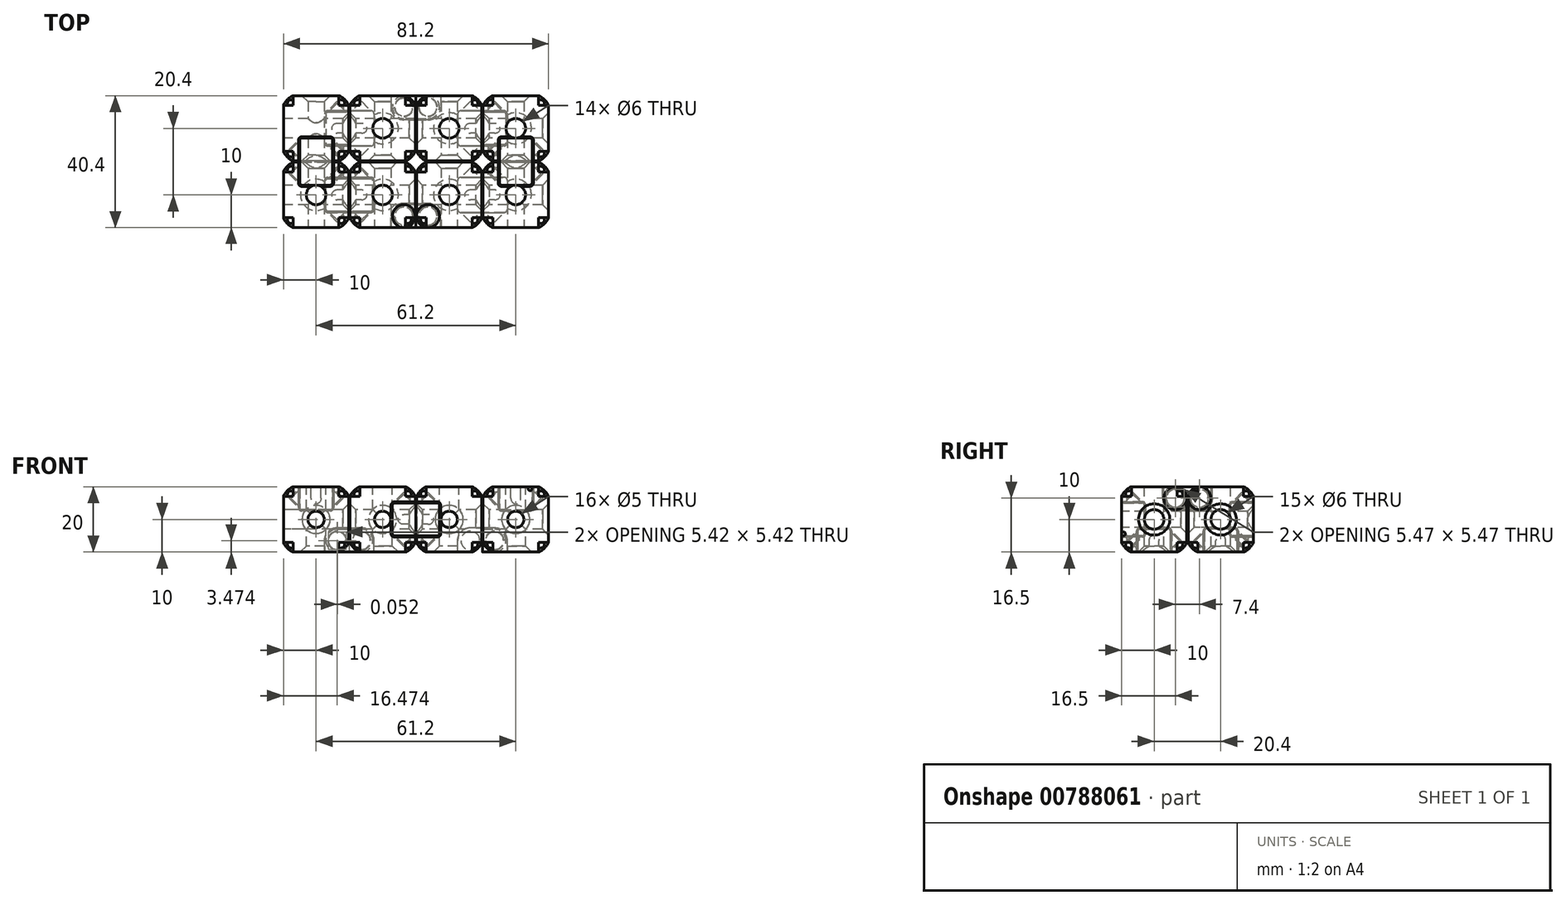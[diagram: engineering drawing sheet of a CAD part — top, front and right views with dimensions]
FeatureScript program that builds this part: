
annotation { "Feature Type Name" : "Feature", "Feature Type Description" : "" }
export const myFeature = defineFeature(function(context is Context, id is Id, definition is map)
    precondition{}
    {
        {
            assignVariable(context, id + "F0", {"name" : "cubeSize", "anyValue" : 20});
        }
        {
            assignVariable(context, id + "F1", {"name" : "hingeSize", "anyValue" : getVariable(context, 'cubeSize') / 2});
        }
        {
            assignVariable(context, id + "F2", {"name" : "hingeDiameter", "anyValue" : getVariable(context, 'hingeSize') / 2});
        }
        {
            assignVariable(context, id + "F3", {"name" : "minThickness", "anyValue" : 1});
        }
        {
            assignVariable(context, id + "F4", {"name" : "hingeGap", "anyValue" : .4});
        }
        {
            var Q0;
            Q0=qCreatedBy(makeId("Top.planeOp"),FACE);
            var sketch = newSketch(context, id + "F5", { "sketchPlane" : qUnion([Q0])});
            skLineSegment(sketch, "E0.bottom", {"start": v(10, -10) * mm, "end": v(-10, -10) * mm});
            skLineSegment(sketch, "E0.top", {"start": v(10, 10) * mm, "end": v(-10, 10) * mm});
            skLineSegment(sketch, "E0.left", {"start": v(10, -10) * mm, "end": v(10, 10) * mm});
            skLineSegment(sketch, "E0.right", {"start": v(-10, -10) * mm, "end": v(-10, 10) * mm});
            skPoint(sketch, "E0.middle", {"position": v(0, 0) * mm});
            skSolve(sketch);
        }
        {
            var Q0;
            Q0=qSketchRegion(id+"F5",true);
            extrude(context, id + "F6", {"entities" : qUnion([Q0]), "depth" : (getVariable(context, 'cubeSize')) * mm, "offsetDistance" : 25 * mm});
        }
        {
            var Q0;
            Q0=qCreatedBy(makeId("Front.planeOp"),FACE);
            var sketch = newSketch(context, id + "F7", { "sketchPlane" : qUnion([Q0])});
            skCircle(sketch, "E1", {"center": v(6.5, 3.5) * mm, "radius": 2.5 * mm});
            skLineSegment(sketch, "E2", {"start": v(6.5, 3.5) * mm, "end": v(9, 3.5) * mm, "construction": true});
            skLineSegment(sketch, "E3", {"start": v(9, 3.5) * mm, "end": v(10, 3.5) * mm, "construction": true});
            skLineSegment(sketch, "E4", {"start": v(6.5, 0) * mm, "end": v(6.5, 1) * mm, "construction": true});
            skLineSegment(sketch, "E5", {"start": v(6.5, 1) * mm, "end": v(6.5, 3.5) * mm, "construction": true});
            skLineSegment(sketch, "E6", {"start": v(10, 0) * mm, "end": v(2.6, 0) * mm});
            skLineSegment(sketch, "E7", {"start": v(2.6, 0) * mm, "end": v(2.6, 3.5) * mm});
            skLineSegment(sketch, "E8", {"start": v(10, 0) * mm, "end": v(10, 7.4) * mm});
            skLineSegment(sketch, "E9", {"start": v(10, 7.4) * mm, "end": v(6.5, 7.4) * mm});
            skArc(sketch, "E10", {"start": v(6.5, 7.4) * mm, "mid": v(3.74, 6.26) * mm, "end": v(2.6, 3.5) * mm});
            skSolve(sketch);
        }
        {
            var Q0;
            Q0=makeQuery(id+"F7.imprint","IMPRINT",FACE,{"disambiguationData":[TD([[makeQuery(id+"F7.imprint","IMPRINT",EDGE,{"derivedFrom":sQuery(id+"F7.wireOp",EDGE,"E1")}),-1.0]])]});
            var Q1;
            Q1=makeQuery(id+"F7.imprint","IMPRINT",FACE,{"disambiguationData":[TD([[makeQuery(id+"F7.imprint","IMPRINT",EDGE,{"derivedFrom":sQuery(id+"F7.wireOp",EDGE,"E1")}),1.0]])]});
            extrude(context, id + "F8", {"entities" : qUnion([Q0, Q1]), "operationType" : NewBodyOperationType.REMOVE, "oppositeDirection" : true, "depth" : (getVariable(context, 'hingeSize') + getVariable(context, 'hingeGap') * 2) * mm, "offsetDistance" : 25 * mm, "symmetric" : true});
        }
        {
            var Q0;
            Q0=makeQuery(id+"F6.opExtrude","CAP_VERTEX",VERTEX,{"disambiguationData":[OSD([sQuery(id+"F5.wireOp",EDGE,"E0.bottom"),sQuery(id+"F5.wireOp",EDGE,"E0.right")])],"isStart":false});
            var Q1;
            Q1=makeQuery(id+"F6.opExtrude","CAP_VERTEX",VERTEX,{"disambiguationData":[OSD([sQuery(id+"F5.wireOp",EDGE,"E0.bottom"),sQuery(id+"F5.wireOp",EDGE,"E0.left")])],"isStart":true});
            var Q2;
            Q2=makeQuery(id+"F6.opExtrude","CAP_VERTEX",VERTEX,{"disambiguationData":[OSD([sQuery(id+"F5.wireOp",EDGE,"E0.top"),sQuery(id+"F5.wireOp",EDGE,"E0.left")])],"isStart":true});
            cPlane(context, id + "F9", {"entities" : qUnion([Q0, Q1, Q2]), "cplaneType" : CPlaneType.THREE_POINT, "offset" : 25 * mm, "width" : 150 * mm, "height" : 150 * mm});
        }
        {
            var Q0;
            Q0=qCreatedBy(id+"F9.planeOp",FACE);
            var sketch = newSketch(context, id + "F10", { "sketchPlane" : qUnion([Q0])});
            skLineSegment(sketch, "E11", {"start": v(5.4, 0.78) * mm, "end": v(-5.4, 0.78) * mm});
            skLineSegment(sketch, "E12", {"start": v(-5.4, 0.78) * mm, "end": v(-8.3, -2.12) * mm});
            skLineSegment(sketch, "E13", {"start": v(-8.3, -2.12) * mm, "end": v(8.3, -2.12) * mm});
            skLineSegment(sketch, "E14", {"start": v(8.3, -2.12) * mm, "end": v(5.4, 0.78) * mm});
            skSolve(sketch);
        }
        {
            var Q0;
            Q0=makeQuery(id+"F10.imprint","IMPRINT",FACE,{"disambiguationData":[TD([[makeQuery(id+"F10.imprint","IMPRINT",EDGE,{"derivedFrom":sQuery(id+"F10.wireOp",EDGE,"E11")}),1.0]])]});
            var Q1;
            Q1=sQuery(id+"F10.wireOp",EDGE,"E13");
            revolve(context, id + "F11", {"operationType" : NewBodyOperationType.REMOVE, "entities" : qUnion([Q0]), "axis" : qUnion([Q1]), "revolveType" : RevolveType.FULL, "oppositeDirection" : true});
        }
        {
            var Q0;
            Q0=qCreatedBy(makeId("Right.planeOp"),FACE);
            var sketch = newSketch(context, id + "F12", { "sketchPlane" : qUnion([Q0])});
            skCircle(sketch, "E15", {"center": v(6.5, 16.5) * mm, "radius": 2.5 * mm});
            skLineSegment(sketch, "E16", {"start": v(2.6, 20) * mm, "end": v(10, 20) * mm});
            skLineSegment(sketch, "E17", {"start": v(10, 20) * mm, "end": v(10, 12.6) * mm});
            skLineSegment(sketch, "E18", {"start": v(10, 12.6) * mm, "end": v(6.5, 12.6) * mm});
            skLineSegment(sketch, "E19", {"start": v(2.6, 20) * mm, "end": v(2.6, 16.5) * mm});
            skLineSegment(sketch, "E20", {"start": v(6.5, 16.5) * mm, "end": v(9, 16.5) * mm, "construction": true});
            skLineSegment(sketch, "E21", {"start": v(9, 16.5) * mm, "end": v(10, 16.5) * mm, "construction": true});
            skLineSegment(sketch, "E22", {"start": v(6.5, 16.5) * mm, "end": v(6.5, 19) * mm, "construction": true});
            skLineSegment(sketch, "E23", {"start": v(6.5, 19) * mm, "end": v(6.5, 20) * mm, "construction": true});
            skArc(sketch, "E24", {"start": v(2.6, 16.5) * mm, "mid": v(3.74, 13.74) * mm, "end": v(6.5, 12.6) * mm});
            skSolve(sketch);
        }
        {
            var Q0;
            Q0=makeQuery(id+"F12.imprint","IMPRINT",FACE,{"disambiguationData":[TD([[makeQuery(id+"F12.imprint","IMPRINT",EDGE,{"derivedFrom":sQuery(id+"F12.wireOp",EDGE,"E15")}),1.0]])]});
            var Q1;
            Q1=makeQuery(id+"F12.imprint","IMPRINT",FACE,{"disambiguationData":[TD([[makeQuery(id+"F12.imprint","IMPRINT",EDGE,{"derivedFrom":sQuery(id+"F12.wireOp",EDGE,"E15")}),-1.0]])]});
            extrude(context, id + "F13", {"entities" : qUnion([Q0, Q1]), "operationType" : NewBodyOperationType.REMOVE, "depth" : (getVariable(context, 'hingeSize') + getVariable(context, 'hingeGap') * 2) * mm, "offsetDistance" : 25 * mm, "symmetric" : true});
        }
        {
            var Q0;
            Q0=makeQuery(id+"F6.opExtrude","CAP_VERTEX",VERTEX,{"disambiguationData":[OSD([sQuery(id+"F5.wireOp",EDGE,"E0.top"),sQuery(id+"F5.wireOp",EDGE,"E0.left")])],"isStart":false});
            var Q1;
            Q1=makeQuery(id+"F6.opExtrude","CAP_VERTEX",VERTEX,{"disambiguationData":[OSD([sQuery(id+"F5.wireOp",EDGE,"E0.top"),sQuery(id+"F5.wireOp",EDGE,"E0.right")])],"isStart":false});
            var Q2;
            Q2=makeQuery(id+"F6.opExtrude","CAP_VERTEX",VERTEX,{"disambiguationData":[OSD([sQuery(id+"F5.wireOp",EDGE,"E0.bottom"),sQuery(id+"F5.wireOp",EDGE,"E0.right")])],"isStart":true});
            cPlane(context, id + "F14", {"entities" : qUnion([Q0, Q1, Q2]), "cplaneType" : CPlaneType.THREE_POINT, "offset" : 25 * mm, "width" : 150 * mm, "height" : 150 * mm});
        }
        {
            var Q0;
            Q0=qCreatedBy(id+"F14.planeOp",FACE);
            var sketch = newSketch(context, id + "F15", { "sketchPlane" : qUnion([Q0])});
            skLineSegment(sketch, "E25", {"start": v(-8.3, 16.26) * mm, "end": v(8.3, 16.26) * mm});
            skLineSegment(sketch, "E26", {"start": v(8.3, 16.26) * mm, "end": v(5.4, 13.36) * mm});
            skLineSegment(sketch, "E27", {"start": v(5.4, 13.36) * mm, "end": v(-5.4, 13.36) * mm});
            skLineSegment(sketch, "E28", {"start": v(-5.4, 13.36) * mm, "end": v(-8.3, 16.26) * mm});
            skSolve(sketch);
        }
        {
            var Q0;
            Q0=qSketchRegion(id+"F15",true);
            var Q1;
            Q1=sQuery(id+"F15.wireOp",EDGE,"E25");
            revolve(context, id + "F16", {"operationType" : NewBodyOperationType.REMOVE, "entities" : qUnion([Q0]), "axis" : qUnion([Q1]), "revolveType" : RevolveType.FULL, "oppositeDirection" : true});
        }
        {
            var Q0;
            Q0=makeQuery(id+"F6.opExtrude","SWEPT_FACE",FACE,{"disambiguationData":[OSD([sQuery(id+"F5.wireOp",EDGE,"E0.right")])]});
            var Q1;
            Q1=makeQuery(id+"F6.opExtrude","SWEPT_FACE",FACE,{"disambiguationData":[OSD([sQuery(id+"F5.wireOp",EDGE,"E0.bottom")])]});
            var Q2;
            {var subQ0=sQuery(id+"F5.wireOp",EDGE,"E0.right");var subQ1=sQuery(id+"F5.wireOp",EDGE,"E0.top");Q2=makeQuery(id+"F13.boolean.opBoolean","SPLIT",EDGE,{"disambiguationData":[TD([makeQuery(id+"F6.opExtrude","SWEPT_FACE",FACE,{"disambiguationData":[OSD([subQ0])]})])],"derivedFrom":makeQuery(id+"F6.opExtrude","CAP_EDGE",EDGE,{"disambiguationData":[OSD([subQ1])],"isStart":false})});}
            var Q3;
            {var subQ0=sQuery(id+"F5.wireOp",EDGE,"E0.left");var subQ1=sQuery(id+"F5.wireOp",EDGE,"E0.top");Q3=makeQuery(id+"F13.boolean.opBoolean","SPLIT",EDGE,{"disambiguationData":[TD([makeQuery(id+"F6.opExtrude","SWEPT_FACE",FACE,{"disambiguationData":[OSD([subQ0])]})])],"derivedFrom":makeQuery(id+"F6.opExtrude","CAP_EDGE",EDGE,{"disambiguationData":[OSD([subQ1])],"isStart":false})});}
            var Q4;
            Q4=makeQuery(id+"F6.opExtrude","CAP_EDGE",EDGE,{"disambiguationData":[OSD([sQuery(id+"F5.wireOp",EDGE,"E0.left")])],"isStart":false});
            var Q5;
            Q5=makeQuery(id+"F6.opExtrude","SWEPT_EDGE",EDGE,{"disambiguationData":[OSD([sQuery(id+"F5.wireOp",EDGE,"E0.top"),sQuery(id+"F5.wireOp",EDGE,"E0.left")])]});
            var Q6;
            {var subQ0=sQuery(id+"F5.wireOp",EDGE,"E0.left");var subQ1=sQuery(id+"F5.wireOp",EDGE,"E0.top");Q6=makeQuery(id+"F8.boolean.opBoolean","SPLIT",EDGE,{"disambiguationData":[TD([makeQuery(id+"F6.opExtrude","SWEPT_FACE",FACE,{"disambiguationData":[OSD([subQ1])]})])],"derivedFrom":makeQuery(id+"F6.opExtrude","CAP_EDGE",EDGE,{"disambiguationData":[OSD([subQ0])],"isStart":true})});}
            var Q7;
            Q7=makeQuery(id+"F6.opExtrude","CAP_EDGE",EDGE,{"disambiguationData":[OSD([sQuery(id+"F5.wireOp",EDGE,"E0.top")])],"isStart":true});
            var Q8;
            {var subQ0=sQuery(id+"F5.wireOp",EDGE,"E0.bottom");var subQ1=sQuery(id+"F5.wireOp",EDGE,"E0.left");Q8=makeQuery(id+"F8.boolean.opBoolean","SPLIT",EDGE,{"disambiguationData":[TD([makeQuery(id+"F6.opExtrude","SWEPT_FACE",FACE,{"disambiguationData":[OSD([subQ0])]})])],"derivedFrom":makeQuery(id+"F6.opExtrude","CAP_EDGE",EDGE,{"disambiguationData":[OSD([subQ1])],"isStart":true})});}
            fillet(context, id + "F17", {"entities" : qUnion([Q0, Q1, Q2, Q3, Q4, Q5, Q6, Q7, Q8]), "radius" : (getVariable(context, 'hingeDiameter') / 2 + getVariable(context, 'minThickness') - .5) * mm, "tangentPropagation" : true, "rho" : .2, "crossSection" : FilletCrossSection.CONIC, "allowEdgeOverflow" : false});
        }
        {
            var Q0;
            Q0=makeQuery(id+"F8.boolean.opBoolean","COPY",EDGE,{"derivedFrom":makeQuery(id+"F8.opExtrude","CAP_EDGE",EDGE,{"disambiguationData":[OSD([sQuery(id+"F7.wireOp",EDGE,"E7")])],"isStart":true})});
            var Q1;
            Q1=makeQuery(id+"F8.boolean.opBoolean","COPY",EDGE,{"derivedFrom":makeQuery(id+"F8.opExtrude","CAP_EDGE",EDGE,{"disambiguationData":[OSD([sQuery(id+"F7.wireOp",EDGE,"E7")])],"isStart":false})});
            var Q2;
            Q2=makeQuery(id+"F13.boolean.opBoolean","COPY",EDGE,{"derivedFrom":makeQuery(id+"F13.opExtrude","CAP_EDGE",EDGE,{"disambiguationData":[OSD([sQuery(id+"F12.wireOp",EDGE,"E18")])],"isStart":false})});
            var Q3;
            Q3=makeQuery(id+"F13.boolean.opBoolean","COPY",EDGE,{"derivedFrom":makeQuery(id+"F13.opExtrude","CAP_EDGE",EDGE,{"disambiguationData":[OSD([sQuery(id+"F12.wireOp",EDGE,"E18")])],"isStart":true})});
            fillet(context, id + "F18", {"entities" : qUnion([Q0, Q1, Q2, Q3]), "radius" : (getVariable(context, 'minThickness')) * mm, "tangentPropagation" : true, "allowEdgeOverflow" : false});
        }
        {
            var Q0;
            Q0=qCreatedBy(makeId("Front.planeOp"),FACE);
            var sketch = newSketch(context, id + "F19", { "sketchPlane" : qUnion([Q0])});
            skCircle(sketch, "E29", {"center": v(6.5, 3.5) * mm, "radius": 2.5 * mm, "construction": true});
            skArc(sketch, "E30", {"start": v(6.5, 7) * mm, "mid": v(3, 3.5) * mm, "end": v(6.5, 0) * mm});
            skArc(sketch, "E31", {"start": v(13.9, 0) * mm, "mid": v(17.4, 3.5) * mm, "end": v(13.9, 7) * mm});
            skLineSegment(sketch, "E32", {"start": v(6.5, 3.5) * mm, "end": v(10, 3.5) * mm, "construction": true});
            skCircle(sketch, "E33", {"center": v(13.9, 3.5) * mm, "radius": 2.5 * mm, "construction": true});
            skLineSegment(sketch, "E34", {"start": v(10, 3.5) * mm, "end": v(10.4, 3.5) * mm, "construction": true});
            skLineSegment(sketch, "E35", {"start": v(10.4, 3.5) * mm, "end": v(13.9, 3.5) * mm, "construction": true});
            skLineSegment(sketch, "E36", {"start": v(10.2, 0) * mm, "end": v(10.2, 3.5) * mm});
            skLineSegment(sketch, "E37", {"start": v(10.2, 3.5) * mm, "end": v(10.2, 7) * mm});
            skLineSegment(sketch, "E38", {"start": v(13.9, 0) * mm, "end": v(6.5, 0) * mm});
            skLineSegment(sketch, "E39", {"start": v(13.9, 7) * mm, "end": v(6.5, 7) * mm});
            skSolve(sketch);
        }
        {
            var Q0;
            Q0=makeQuery(id+"F19.imprint","IMPRINT",FACE,{"disambiguationData":[TD([[makeQuery(id+"F19.imprint","IMPRINT",EDGE,{"derivedFrom":sQuery(id+"F19.wireOp",EDGE,"E30")}),1.0]])]});
            extrude(context, id + "F20", {"entities" : qUnion([Q0]), "depth" : (getVariable(context, 'hingeSize')) * mm, "offsetDistance" : 25 * mm, "symmetric" : true});
        }
        {
            var Q0;
            Q0=qCreatedBy(id+"F9.planeOp",FACE);
            var sketch = newSketch(context, id + "F21", { "sketchPlane" : qUnion([Q0])});
            skLineSegment(sketch, "E40", {"start": v(7.73, -2.12) * mm, "end": v(4.83, 0.78) * mm});
            skLineSegment(sketch, "E41", {"start": v(4.83, 0.78) * mm, "end": v(-4.83, 0.78) * mm});
            skLineSegment(sketch, "E42", {"start": v(-4.83, 0.78) * mm, "end": v(-7.73, -2.12) * mm});
            skLineSegment(sketch, "E43", {"start": v(-7.73, -2.12) * mm, "end": v(7.73, -2.12) * mm});
            skSolve(sketch);
        }
        {
            var Q0;
            Q0=qSketchRegion(id+"F21",true);
            var Q1;
            Q1=sQuery(id+"F21.wireOp",EDGE,"E43");
            revolve(context, id + "F22", {"operationType" : NewBodyOperationType.ADD, "entities" : qUnion([Q0]), "axis" : qUnion([Q1]), "revolveType" : RevolveType.FULL});
        }
        {
            var Q0;
            Q0=qCreatedBy(makeId("Right.planeOp"),FACE);
            var sketch = newSketch(context, id + "F23", { "sketchPlane" : qUnion([Q0])});
            skCircle(sketch, "E44", {"center": v(6.5, 16.5) * mm, "radius": 2.9 * mm, "construction": true});
            skArc(sketch, "E45", {"start": v(6.5, 20) * mm, "mid": v(3, 16.5) * mm, "end": v(6.5, 13) * mm});
            skArc(sketch, "E46", {"start": v(13.9, 13) * mm, "mid": v(17.4, 16.5) * mm, "end": v(13.9, 20) * mm});
            skLineSegment(sketch, "E47", {"start": v(6.5, 16.5) * mm, "end": v(10, 16.5) * mm, "construction": true});
            skCircle(sketch, "E48", {"center": v(13.9, 16.5) * mm, "radius": 2.5 * mm, "construction": true});
            skLineSegment(sketch, "E49", {"start": v(10, 16.5) * mm, "end": v(10.4, 16.5) * mm, "construction": true});
            skLineSegment(sketch, "E50", {"start": v(10.4, 16.5) * mm, "end": v(13.9, 16.5) * mm, "construction": true});
            skLineSegment(sketch, "E51", {"start": v(10.2, 13) * mm, "end": v(10.2, 16.5) * mm});
            skLineSegment(sketch, "E52", {"start": v(10.2, 16.5) * mm, "end": v(10.2, 20) * mm});
            skLineSegment(sketch, "E53", {"start": v(13.9, 13) * mm, "end": v(6.5, 13) * mm});
            skLineSegment(sketch, "E54", {"start": v(13.9, 20) * mm, "end": v(6.5, 20) * mm});
            skSolve(sketch);
        }
        {
            var Q0;
            {var subQ3=sQuery(id+"F23.wireOp",EDGE,"E45");Q0=makeQuery(id+"F23.imprint","IMPRINT",FACE,{"disambiguationData":[TD([[makeQuery(id+"F23.imprint","IMPRINT",EDGE,{"derivedFrom":subQ3}),1.0]])]});}
            extrude(context, id + "F24", {"entities" : qUnion([Q0]), "depth" : (getVariable(context, 'hingeSize')) * mm, "offsetDistance" : 25 * mm, "symmetric" : true});
        }
        {
            var Q0;
            Q0=makeQuery(id+"F20.opExtrude","CAP_EDGE",EDGE,{"disambiguationData":[OSD([sQuery(id+"F19.wireOp",EDGE,"E38")])],"isStart":false});
            var Q1;
            Q1=makeQuery(id+"F20.opExtrude","CAP_EDGE",EDGE,{"disambiguationData":[OSD([sQuery(id+"F19.wireOp",EDGE,"E38")])],"isStart":true});
            var Q2;
            Q2=makeQuery(id+"F24.opExtrude","CAP_EDGE",EDGE,{"disambiguationData":[OSD([sQuery(id+"F23.wireOp",EDGE,"E54")])],"isStart":false});
            var Q3;
            Q3=makeQuery(id+"F24.opExtrude","CAP_EDGE",EDGE,{"disambiguationData":[OSD([sQuery(id+"F23.wireOp",EDGE,"E54")])],"isStart":true});
            fillet(context, id + "F25", {"entities" : qUnion([Q0, Q1, Q2, Q3]), "radius" : (getVariable(context, 'minThickness') - getVariable(context, 'hingeGap')) * mm, "tangentPropagation" : true, "allowEdgeOverflow" : false});
        }
        {
            var Q0;
            Q0=qCreatedBy(id+"F14.planeOp",FACE);
            var sketch = newSketch(context, id + "F26", { "sketchPlane" : qUnion([Q0])});
            skLineSegment(sketch, "E55", {"start": v(-7.73, 16.26) * mm, "end": v(7.73, 16.26) * mm});
            skLineSegment(sketch, "E56", {"start": v(7.73, 16.26) * mm, "end": v(4.83, 13.36) * mm});
            skLineSegment(sketch, "E57", {"start": v(4.83, 13.36) * mm, "end": v(-4.83, 13.36) * mm});
            skLineSegment(sketch, "E58", {"start": v(-4.83, 13.36) * mm, "end": v(-7.73, 16.26) * mm});
            skSolve(sketch);
        }
        {
            var Q0;
            Q0=makeQuery(id+"F26.imprint","IMPRINT",FACE,{"disambiguationData":[TD([[makeQuery(id+"F26.imprint","IMPRINT",EDGE,{"derivedFrom":sQuery(id+"F26.wireOp",EDGE,"E55")}),-1.0]])]});
            var Q1;
            Q1=sQuery(id+"F26.wireOp",EDGE,"E55");
            revolve(context, id + "F27", {"operationType" : NewBodyOperationType.ADD, "entities" : qUnion([Q0]), "axis" : qUnion([Q1]), "revolveType" : RevolveType.FULL});
        }
        {
            var Q0;
            Q0=makeQuery(id+"F20.opExtrude","SWEPT_FACE",FACE,{"disambiguationData":[OSD([sQuery(id+"F19.wireOp",EDGE,"E36"),sQuery(id+"F19.wireOp",EDGE,"E37")])]});
            var sketch = newSketch(context, id + "F28", { "sketchPlane" : qUnion([Q0])});
            skLineSegment(sketch, "E59", {"start": v(-7.63, -0.2) * mm, "end": v(6.67, -0.2) * mm, "construction": true});
            skSolve(sketch);
        }
        {
            var Q0;
            Q0=makeQuery(id+"F6.opExtrude","SWEPT_BODY",BODY,{"disambiguationData":[OSD([sQuery(id+"F5.wireOp",EDGE,"E0.bottom"),sQuery(id+"F5.wireOp",EDGE,"E0.top"),sQuery(id+"F5.wireOp",EDGE,"E0.left"),sQuery(id+"F5.wireOp",EDGE,"E0.right")])]});
            var Q1;
            Q1=makeQuery(id+"F24.opExtrude","SWEPT_BODY",BODY,{"disambiguationData":[OSD([sQuery(id+"F23.wireOp",EDGE,"E45"),sQuery(id+"F23.wireOp",EDGE,"E51"),sQuery(id+"F23.wireOp",EDGE,"E52"),sQuery(id+"F23.wireOp",EDGE,"E53"),sQuery(id+"F23.wireOp",EDGE,"E54")])]});
            var Q2;
            Q2=sQuery(id+"F28.wireOp",EDGE,"E59");
            circularPattern(context, id + "F29", {"entities" : qUnion([Q0, Q1]), "axis" : qUnion([Q2]), "angle" : 90 * degree, "instanceCount" : 2});
        }
        {
            var Q0;
            Q0=makeQuery(id+"F29.opPattern","COPY",BODY,{"derivedFrom":makeQuery(id+"F6.opExtrude","SWEPT_BODY",BODY,{"disambiguationData":[OSD([sQuery(id+"F5.wireOp",EDGE,"E0.bottom"),sQuery(id+"F5.wireOp",EDGE,"E0.top"),sQuery(id+"F5.wireOp",EDGE,"E0.left"),sQuery(id+"F5.wireOp",EDGE,"E0.right")])]}),"instanceName":"1"});
            var Q1;
            Q1=makeQuery(id+"F29.opPattern","COPY",BODY,{"derivedFrom":makeQuery(id+"F24.opExtrude","SWEPT_BODY",BODY,{"disambiguationData":[OSD([sQuery(id+"F23.wireOp",EDGE,"E45"),sQuery(id+"F23.wireOp",EDGE,"E51"),sQuery(id+"F23.wireOp",EDGE,"E52"),sQuery(id+"F23.wireOp",EDGE,"E53"),sQuery(id+"F23.wireOp",EDGE,"E54")])]}),"instanceName":"1"});
            var Q2;
            Q2=qCreatedBy(makeId("Front.planeOp"),FACE);
            mirror(context, id + "F30", {"entities" : qUnion([Q0, Q1]), "mirrorPlane" : qUnion([Q2])});
        }
        {
            var Q0;
            Q0=makeQuery(id+"F29.opPattern","COPY",BODY,{"derivedFrom":makeQuery(id+"F24.opExtrude","SWEPT_BODY",BODY,{"disambiguationData":[OSD([sQuery(id+"F23.wireOp",EDGE,"E45"),sQuery(id+"F23.wireOp",EDGE,"E51"),sQuery(id+"F23.wireOp",EDGE,"E52"),sQuery(id+"F23.wireOp",EDGE,"E53"),sQuery(id+"F23.wireOp",EDGE,"E54")])]}),"instanceName":"1"});
            var Q1;
            Q1=makeQuery(id+"F29.opPattern","COPY",BODY,{"derivedFrom":makeQuery(id+"F6.opExtrude","SWEPT_BODY",BODY,{"disambiguationData":[OSD([sQuery(id+"F5.wireOp",EDGE,"E0.bottom"),sQuery(id+"F5.wireOp",EDGE,"E0.top"),sQuery(id+"F5.wireOp",EDGE,"E0.left"),sQuery(id+"F5.wireOp",EDGE,"E0.right")])]}),"instanceName":"1"});
            deleteBodies(context, id + "F31", {"entities" : qUnion([Q0, Q1])});
        }
        {
            var Q0;
            Q0=makeQuery(id+"F20.opExtrude","SWEPT_BODY",BODY,{"disambiguationData":[OSD([sQuery(id+"F19.wireOp",EDGE,"E30"),sQuery(id+"F19.wireOp",EDGE,"E36"),sQuery(id+"F19.wireOp",EDGE,"E37"),sQuery(id+"F19.wireOp",EDGE,"E38"),sQuery(id+"F19.wireOp",EDGE,"E39")])]});
            var Q1;
            Q1=makeQuery(id+"F20.opExtrude","SWEPT_FACE",FACE,{"disambiguationData":[OSD([sQuery(id+"F19.wireOp",EDGE,"E36"),sQuery(id+"F19.wireOp",EDGE,"E37")])]});
            mirror(context, id + "F32", {"operationType" : NewBodyOperationType.ADD, "entities" : qUnion([Q0]), "mirrorPlane" : qUnion([Q1])});
        }
        {
            var Q0;
            {var subQ0=sQuery(id+"F5.wireOp",EDGE,"E0.left");var subQ1=makeQuery(id+"F6.opExtrude","SWEPT_FACE",FACE,{"disambiguationData":[OSD([subQ0])]});var subQ2=sQuery(id+"F5.wireOp",EDGE,"E0.bottom");Q0=makeQuery(id+"F30.opPattern","COPY",VERTEX,{"derivedFrom":makeQuery(id+"F29.opPattern","COPY",VERTEX,{"derivedFrom":makeQuery(id+"F17.opFillet","BLEND_VERTEX",VERTEX,{"blendedFrom":[makeQuery(id+"F6.opExtrude","CAP_VERTEX",VERTEX,{"disambiguationData":[OSD([subQ2,subQ0])],"isStart":true}),makeQuery(id+"F6.opExtrude","SWEPT_EDGE",EDGE,{"disambiguationData":[OSD([subQ2,subQ0])]}),makeQuery(id+"F8.boolean.opBoolean","SPLIT",EDGE,{"disambiguationData":[TD([makeQuery(id+"F6.opExtrude","SWEPT_FACE",FACE,{"disambiguationData":[OSD([subQ2])]})])],"derivedFrom":makeQuery(id+"F6.opExtrude","CAP_EDGE",EDGE,{"disambiguationData":[OSD([subQ0])],"isStart":true})}),subQ1],"blendedInto":[subQ1]}),"instanceName":"1"}),"instanceName":"1"});}
            var Q1;
            {var subQ0=sQuery(id+"F5.wireOp",EDGE,"E0.left");var subQ1=sQuery(id+"F5.wireOp",EDGE,"E0.top");Q1=makeQuery(id+"F30.opPattern","COPY",VERTEX,{"derivedFrom":makeQuery(id+"F29.opPattern","COPY",VERTEX,{"derivedFrom":makeQuery(id+"F17.opFillet","BLEND_VERTEX",VERTEX,{"blendedFrom":[makeQuery(id+"F6.opExtrude","CAP_VERTEX",VERTEX,{"disambiguationData":[OSD([subQ1,subQ0])],"isStart":false}),makeQuery(id+"F6.opExtrude","SWEPT_EDGE",EDGE,{"disambiguationData":[OSD([subQ1,subQ0])]}),makeQuery(id+"F6.opExtrude","CAP_EDGE",EDGE,{"disambiguationData":[OSD([subQ0])],"isStart":false}),makeQuery(id+"F6.opExtrude","SWEPT_FACE",FACE,{"disambiguationData":[OSD([subQ0])]})],"blendedInto":[makeQuery(id+"F6.opExtrude","SWEPT_FACE",FACE,{"disambiguationData":[OSD([subQ0])]})]}),"instanceName":"1"}),"instanceName":"1"});}
            var Q2;
            {var subQ0=sQuery(id+"F5.wireOp",EDGE,"E0.right");var subQ1=sQuery(id+"F5.wireOp",EDGE,"E0.top");Q2=makeQuery(id+"F30.opPattern","COPY",VERTEX,{"derivedFrom":makeQuery(id+"F29.opPattern","COPY",VERTEX,{"derivedFrom":makeQuery(id+"F17.opFillet","BLEND_VERTEX",VERTEX,{"blendedFrom":[makeQuery(id+"F6.opExtrude","CAP_VERTEX",VERTEX,{"disambiguationData":[OSD([subQ1,subQ0])],"isStart":false}),makeQuery(id+"F6.opExtrude","SWEPT_EDGE",EDGE,{"disambiguationData":[OSD([subQ1,subQ0])]}),makeQuery(id+"F6.opExtrude","CAP_EDGE",EDGE,{"disambiguationData":[OSD([subQ0])],"isStart":false}),makeQuery(id+"F6.opExtrude","SWEPT_FACE",FACE,{"disambiguationData":[OSD([subQ0])]})],"blendedInto":[makeQuery(id+"F6.opExtrude","SWEPT_FACE",FACE,{"disambiguationData":[OSD([subQ0])]})]}),"instanceName":"1"}),"instanceName":"1"});}
            cPlane(context, id + "F33", {"entities" : qUnion([Q0, Q1, Q2]), "cplaneType" : CPlaneType.THREE_POINT, "offset" : 25 * mm, "width" : 150 * mm, "height" : 150 * mm});
        }
        {
            var Q0;
            Q0=qCreatedBy(id+"F33.planeOp",FACE);
            var sketch = newSketch(context, id + "F34", { "sketchPlane" : qUnion([Q0])});
            skLineSegment(sketch, "E60", {"start": v(-23.62, 17.73) * mm, "end": v(-23.62, 2.27) * mm, "construction": true});
            skSolve(sketch);
        }
        {
            var Q0;
            Q0=makeQuery(id+"F30.opPattern","COPY",BODY,{"derivedFrom":makeQuery(id+"F29.opPattern","COPY",BODY,{"derivedFrom":makeQuery(id+"F24.opExtrude","SWEPT_BODY",BODY,{"disambiguationData":[OSD([sQuery(id+"F23.wireOp",EDGE,"E45"),sQuery(id+"F23.wireOp",EDGE,"E51"),sQuery(id+"F23.wireOp",EDGE,"E52"),sQuery(id+"F23.wireOp",EDGE,"E53"),sQuery(id+"F23.wireOp",EDGE,"E54")])]}),"instanceName":"1"}),"instanceName":"1"});
            var Q1;
            Q1=sQuery(id+"F34.wireOp",EDGE,"E60");
            circularPattern(context, id + "F35", {"entities" : qUnion([Q0]), "axis" : qUnion([Q1]), "angle" : 90 * degree, "instanceCount" : 2, "oppositeDirection" : true});
        }
        {
            var Q0;
            Q0=makeQuery(id+"F30.opPattern","COPY",BODY,{"derivedFrom":makeQuery(id+"F29.opPattern","COPY",BODY,{"derivedFrom":makeQuery(id+"F24.opExtrude","SWEPT_BODY",BODY,{"disambiguationData":[OSD([sQuery(id+"F23.wireOp",EDGE,"E45"),sQuery(id+"F23.wireOp",EDGE,"E51"),sQuery(id+"F23.wireOp",EDGE,"E52"),sQuery(id+"F23.wireOp",EDGE,"E53"),sQuery(id+"F23.wireOp",EDGE,"E54")])]}),"instanceName":"1"}),"instanceName":"1"});
            deleteBodies(context, id + "F36", {"entities" : qUnion([Q0])});
        }
        {
            var Q0;
            Q0=makeQuery(id+"F24.opExtrude","SWEPT_BODY",BODY,{"disambiguationData":[OSD([sQuery(id+"F23.wireOp",EDGE,"E45"),sQuery(id+"F23.wireOp",EDGE,"E51"),sQuery(id+"F23.wireOp",EDGE,"E52"),sQuery(id+"F23.wireOp",EDGE,"E53"),sQuery(id+"F23.wireOp",EDGE,"E54")])]});
            var Q1;
            Q1=makeQuery(id+"F6.opExtrude","SWEPT_BODY",BODY,{"disambiguationData":[OSD([sQuery(id+"F5.wireOp",EDGE,"E0.bottom"),sQuery(id+"F5.wireOp",EDGE,"E0.top"),sQuery(id+"F5.wireOp",EDGE,"E0.left"),sQuery(id+"F5.wireOp",EDGE,"E0.right")])]});
            var Q2;
            Q2=makeQuery(id+"F20.opExtrude","SWEPT_BODY",BODY,{"disambiguationData":[OSD([sQuery(id+"F19.wireOp",EDGE,"E30"),sQuery(id+"F19.wireOp",EDGE,"E36"),sQuery(id+"F19.wireOp",EDGE,"E37"),sQuery(id+"F19.wireOp",EDGE,"E38"),sQuery(id+"F19.wireOp",EDGE,"E39")])]});
            var Q3;
            Q3=makeQuery(id+"F30.opPattern","COPY",BODY,{"derivedFrom":makeQuery(id+"F29.opPattern","COPY",BODY,{"derivedFrom":makeQuery(id+"F6.opExtrude","SWEPT_BODY",BODY,{"disambiguationData":[OSD([sQuery(id+"F5.wireOp",EDGE,"E0.bottom"),sQuery(id+"F5.wireOp",EDGE,"E0.top"),sQuery(id+"F5.wireOp",EDGE,"E0.left"),sQuery(id+"F5.wireOp",EDGE,"E0.right")])]}),"instanceName":"1"}),"instanceName":"1"});
            var Q4;
            Q4=makeQuery(id+"F35.opPattern","COPY",BODY,{"derivedFrom":makeQuery(id+"F30.opPattern","COPY",BODY,{"derivedFrom":makeQuery(id+"F29.opPattern","COPY",BODY,{"derivedFrom":makeQuery(id+"F24.opExtrude","SWEPT_BODY",BODY,{"disambiguationData":[OSD([sQuery(id+"F23.wireOp",EDGE,"E45"),sQuery(id+"F23.wireOp",EDGE,"E51"),sQuery(id+"F23.wireOp",EDGE,"E52"),sQuery(id+"F23.wireOp",EDGE,"E53"),sQuery(id+"F23.wireOp",EDGE,"E54")])]}),"instanceName":"1"}),"instanceName":"1"}),"instanceName":"1"});
            var Q5;
            Q5=makeQuery(id+"F24.opExtrude","SWEPT_FACE",FACE,{"disambiguationData":[OSD([sQuery(id+"F23.wireOp",EDGE,"E51"),sQuery(id+"F23.wireOp",EDGE,"E52")])]});
            mirror(context, id + "F37", {"operationType" : NewBodyOperationType.ADD, "entities" : qUnion([Q0, Q1, Q2, Q3, Q4]), "mirrorPlane" : qUnion([Q5])});
        }
        {
            var Q0;
            Q0=makeQuery(id+"F35.opPattern","COPY",BODY,{"derivedFrom":makeQuery(id+"F30.opPattern","COPY",BODY,{"derivedFrom":makeQuery(id+"F29.opPattern","COPY",BODY,{"derivedFrom":makeQuery(id+"F24.opExtrude","SWEPT_BODY",BODY,{"disambiguationData":[OSD([sQuery(id+"F23.wireOp",EDGE,"E45"),sQuery(id+"F23.wireOp",EDGE,"E51"),sQuery(id+"F23.wireOp",EDGE,"E52"),sQuery(id+"F23.wireOp",EDGE,"E53"),sQuery(id+"F23.wireOp",EDGE,"E54")])]}),"instanceName":"1"}),"instanceName":"1"}),"instanceName":"1"});
            var Q1;
            Q1=makeQuery(id+"F37.opPattern","COPY",BODY,{"derivedFrom":makeQuery(id+"F35.opPattern","COPY",BODY,{"derivedFrom":makeQuery(id+"F30.opPattern","COPY",BODY,{"derivedFrom":makeQuery(id+"F29.opPattern","COPY",BODY,{"derivedFrom":makeQuery(id+"F24.opExtrude","SWEPT_BODY",BODY,{"disambiguationData":[OSD([sQuery(id+"F23.wireOp",EDGE,"E45"),sQuery(id+"F23.wireOp",EDGE,"E51"),sQuery(id+"F23.wireOp",EDGE,"E52"),sQuery(id+"F23.wireOp",EDGE,"E53"),sQuery(id+"F23.wireOp",EDGE,"E54")])]}),"instanceName":"1"}),"instanceName":"1"}),"instanceName":"1"}),"instanceName":"1"});
            var Q2;
            Q2=makeQuery(id+"F24.opExtrude","SWEPT_BODY",BODY,{"disambiguationData":[OSD([sQuery(id+"F23.wireOp",EDGE,"E45"),sQuery(id+"F23.wireOp",EDGE,"E51"),sQuery(id+"F23.wireOp",EDGE,"E52"),sQuery(id+"F23.wireOp",EDGE,"E53"),sQuery(id+"F23.wireOp",EDGE,"E54")])]});
            var Q3;
            Q3=makeQuery(id+"F37.opPattern","COPY",BODY,{"derivedFrom":makeQuery(id+"F20.opExtrude","SWEPT_BODY",BODY,{"disambiguationData":[OSD([sQuery(id+"F19.wireOp",EDGE,"E30"),sQuery(id+"F19.wireOp",EDGE,"E36"),sQuery(id+"F19.wireOp",EDGE,"E37"),sQuery(id+"F19.wireOp",EDGE,"E38"),sQuery(id+"F19.wireOp",EDGE,"E39")])]}),"instanceName":"1"});
            var Q4;
            Q4=makeQuery(id+"F20.opExtrude","SWEPT_BODY",BODY,{"disambiguationData":[OSD([sQuery(id+"F19.wireOp",EDGE,"E30"),sQuery(id+"F19.wireOp",EDGE,"E36"),sQuery(id+"F19.wireOp",EDGE,"E37"),sQuery(id+"F19.wireOp",EDGE,"E38"),sQuery(id+"F19.wireOp",EDGE,"E39")])]});
            var Q5;
            Q5=makeQuery(id+"F37.opPattern","COPY",BODY,{"derivedFrom":makeQuery(id+"F30.opPattern","COPY",BODY,{"derivedFrom":makeQuery(id+"F29.opPattern","COPY",BODY,{"derivedFrom":makeQuery(id+"F6.opExtrude","SWEPT_BODY",BODY,{"disambiguationData":[OSD([sQuery(id+"F5.wireOp",EDGE,"E0.bottom"),sQuery(id+"F5.wireOp",EDGE,"E0.top"),sQuery(id+"F5.wireOp",EDGE,"E0.left"),sQuery(id+"F5.wireOp",EDGE,"E0.right")])]}),"instanceName":"1"}),"instanceName":"1"}),"instanceName":"1"});
            var Q6;
            Q6=makeQuery(id+"F37.opPattern","COPY",BODY,{"derivedFrom":makeQuery(id+"F6.opExtrude","SWEPT_BODY",BODY,{"disambiguationData":[OSD([sQuery(id+"F5.wireOp",EDGE,"E0.bottom"),sQuery(id+"F5.wireOp",EDGE,"E0.top"),sQuery(id+"F5.wireOp",EDGE,"E0.left"),sQuery(id+"F5.wireOp",EDGE,"E0.right")])]}),"instanceName":"1"});
            var Q7;
            Q7=makeQuery(id+"F6.opExtrude","SWEPT_BODY",BODY,{"disambiguationData":[OSD([sQuery(id+"F5.wireOp",EDGE,"E0.bottom"),sQuery(id+"F5.wireOp",EDGE,"E0.top"),sQuery(id+"F5.wireOp",EDGE,"E0.left"),sQuery(id+"F5.wireOp",EDGE,"E0.right")])]});
            var Q8;
            Q8=makeQuery(id+"F30.opPattern","COPY",BODY,{"derivedFrom":makeQuery(id+"F29.opPattern","COPY",BODY,{"derivedFrom":makeQuery(id+"F6.opExtrude","SWEPT_BODY",BODY,{"disambiguationData":[OSD([sQuery(id+"F5.wireOp",EDGE,"E0.bottom"),sQuery(id+"F5.wireOp",EDGE,"E0.top"),sQuery(id+"F5.wireOp",EDGE,"E0.left"),sQuery(id+"F5.wireOp",EDGE,"E0.right")])]}),"instanceName":"1"}),"instanceName":"1"});
            var Q9;
            Q9=makeQuery(id+"F35.opPattern","COPY",FACE,{"derivedFrom":makeQuery(id+"F30.opPattern","COPY",FACE,{"derivedFrom":makeQuery(id+"F29.opPattern","COPY",FACE,{"derivedFrom":makeQuery(id+"F24.opExtrude","SWEPT_FACE",FACE,{"disambiguationData":[OSD([sQuery(id+"F23.wireOp",EDGE,"E51"),sQuery(id+"F23.wireOp",EDGE,"E52")])]}),"instanceName":"1"}),"instanceName":"1"}),"instanceName":"1"});
            mirror(context, id + "F38", {"operationType" : NewBodyOperationType.ADD, "entities" : qUnion([Q0, Q1, Q2, Q3, Q4, Q5, Q6, Q7, Q8]), "mirrorPlane" : qUnion([Q9])});
        }
        {
            var Q0;
            Q0=makeQuery(id+"F6.opExtrude","SWEPT_FACE",FACE,{"disambiguationData":[OSD([sQuery(id+"F5.wireOp",EDGE,"E0.bottom")])]});
            var sketch = newSketch(context, id + "F39", { "sketchPlane" : qUnion([Q0])});
            skCircle(sketch, "E61", {"center": v(20.4, 10) * mm, "radius": 2.5 * mm});
            skCircle(sketch, "E62", {"center": v(0, 10) * mm, "radius": 2.5 * mm});
            skCircle(sketch, "E63", {"center": v(40.8, 10) * mm, "radius": 2.5 * mm});
            skCircle(sketch, "E64", {"center": v(61.2, 10) * mm, "radius": 2.5 * mm});
            skSolve(sketch);
        }
        {
            var Q0;
            Q0=makeQuery(id+"F39.imprint","IMPRINT",FACE,{"disambiguationData":[TD([[makeQuery(id+"F39.imprint","IMPRINT",EDGE,{"derivedFrom":sQuery(id+"F39.wireOp",EDGE,"E61")}),1.0]])]});
            var Q1;
            Q1=makeQuery(id+"F39.imprint","IMPRINT",FACE,{"disambiguationData":[TD([[makeQuery(id+"F39.imprint","IMPRINT",EDGE,{"derivedFrom":sQuery(id+"F39.wireOp",EDGE,"E62")}),1.0]])]});
            var Q2;
            Q2=makeQuery(id+"F39.imprint","IMPRINT",FACE,{"disambiguationData":[TD([[makeQuery(id+"F39.imprint","IMPRINT",EDGE,{"derivedFrom":sQuery(id+"F39.wireOp",EDGE,"E63")}),1.0]])]});
            var Q3;
            Q3=makeQuery(id+"F39.imprint","IMPRINT",FACE,{"disambiguationData":[TD([[makeQuery(id+"F39.imprint","IMPRINT",EDGE,{"derivedFrom":sQuery(id+"F39.wireOp",EDGE,"E64")}),1.0]])]});
            extrude(context, id + "F40", {"entities" : qUnion([Q0, Q1, Q2, Q3]), "operationType" : NewBodyOperationType.REMOVE, "endBound" : BoundingType.THROUGH_ALL, "oppositeDirection" : true, "depth" : 25 * mm, "offsetDistance" : 25 * mm});
        }
        {
            var Q0;
            Q0=makeQuery(id+"F37.opPattern","COPY",FACE,{"derivedFrom":makeQuery(id+"F6.opExtrude","SWEPT_FACE",FACE,{"disambiguationData":[OSD([sQuery(id+"F5.wireOp",EDGE,"E0.right")])]}),"instanceName":"1"});
            var sketch = newSketch(context, id + "F41", { "sketchPlane" : qUnion([Q0])});
            skCircle(sketch, "E65", {"center": v(-20.4, 10) * mm, "radius": 3 * mm});
            skCircle(sketch, "E66", {"center": v(0, 10) * mm, "radius": 3 * mm});
            skSolve(sketch);
        }
        {
            var Q0;
            Q0=makeQuery(id+"F41.imprint","IMPRINT",FACE,{"disambiguationData":[TD([[makeQuery(id+"F41.imprint","IMPRINT",EDGE,{"derivedFrom":sQuery(id+"F41.wireOp",EDGE,"E65")}),1.0]])]});
            var Q1;
            Q1=makeQuery(id+"F41.imprint","IMPRINT",FACE,{"disambiguationData":[TD([[makeQuery(id+"F41.imprint","IMPRINT",EDGE,{"derivedFrom":sQuery(id+"F41.wireOp",EDGE,"E66")}),1.0]])]});
            extrude(context, id + "F42", {"entities" : qUnion([Q0, Q1]), "operationType" : NewBodyOperationType.REMOVE, "endBound" : BoundingType.THROUGH_ALL, "oppositeDirection" : true, "depth" : 25 * mm, "offsetDistance" : 25 * mm});
        }
        {
            var Q0;
            Q0=makeQuery(id+"F37.opPattern","COPY",FACE,{"derivedFrom":makeQuery(id+"F6.opExtrude","CAP_FACE",FACE,{"disambiguationData":[OSD([sQuery(id+"F5.wireOp",EDGE,"E0.bottom"),sQuery(id+"F5.wireOp",EDGE,"E0.top"),sQuery(id+"F5.wireOp",EDGE,"E0.left"),sQuery(id+"F5.wireOp",EDGE,"E0.right")])],"isStart":false}),"instanceName":"1"});
            var sketch = newSketch(context, id + "F43", { "sketchPlane" : qUnion([Q0])});
            skCircle(sketch, "E67", {"center": v(0, 20.4) * mm, "radius": 3 * mm});
            skCircle(sketch, "E68", {"center": v(20.4, 20.4) * mm, "radius": 3 * mm});
            skCircle(sketch, "E69", {"center": v(40.8, 20.4) * mm, "radius": 3 * mm});
            skCircle(sketch, "E70", {"center": v(61.2, 20.4) * mm, "radius": 3 * mm});
            skCircle(sketch, "E71", {"center": v(0, 0) * mm, "radius": 3 * mm});
            skCircle(sketch, "E72", {"center": v(20.4, 0) * mm, "radius": 3 * mm});
            skCircle(sketch, "E73", {"center": v(40.8, 0) * mm, "radius": 3 * mm});
            skCircle(sketch, "E74", {"center": v(61.2, 0) * mm, "radius": 3 * mm});
            skSolve(sketch);
        }
        {
            var Q0;
            {var subQ2=sQuery(id+"F12.wireOp",EDGE,"E19");var subQ7=makeQuery(id+"F37.opPattern","COPY",EDGE,{"derivedFrom":makeQuery(id+"F13.boolean.opBoolean","COPY",EDGE,{"derivedFrom":makeQuery(id+"F13.opExtrude","SWEPT_EDGE",EDGE,{"disambiguationData":[OSD([sQuery(id+"F12.wireOp",EDGE,"E16"),subQ2])]})}),"instanceName":"1"});Q0=makeQuery(id+"F43.imprint","IMPRINT",FACE,{"disambiguationData":[TD([[makeQuery(id+"F43.imprint","IMPRINT",EDGE,{"derivedFrom":subQ7}),-1.0]])]});}
            var Q1;
            {var subQ2=sQuery(id+"F12.wireOp",EDGE,"E19");var subQ7=makeQuery(id+"F37.opPattern","COPY",EDGE,{"derivedFrom":makeQuery(id+"F13.boolean.opBoolean","COPY",EDGE,{"derivedFrom":makeQuery(id+"F13.opExtrude","SWEPT_EDGE",EDGE,{"disambiguationData":[OSD([sQuery(id+"F12.wireOp",EDGE,"E16"),subQ2])]})}),"instanceName":"1"});Q1=makeQuery(id+"F43.imprint","IMPRINT",FACE,{"disambiguationData":[TD([[makeQuery(id+"F43.imprint","IMPRINT",EDGE,{"derivedFrom":subQ7}),1.0]])]});}
            var Q2;
            Q2=makeQuery(id+"F43.imprint","IMPRINT",FACE,{"disambiguationData":[TD([[makeQuery(id+"F43.imprint","IMPRINT",EDGE,{"derivedFrom":sQuery(id+"F43.wireOp",EDGE,"E71")}),1.0]])]});
            var Q3;
            Q3=makeQuery(id+"F43.imprint","IMPRINT",FACE,{"disambiguationData":[TD([[makeQuery(id+"F43.imprint","IMPRINT",EDGE,{"derivedFrom":sQuery(id+"F43.wireOp",EDGE,"E68")}),1.0]])]});
            var Q4;
            Q4=makeQuery(id+"F43.imprint","IMPRINT",FACE,{"disambiguationData":[TD([[makeQuery(id+"F43.imprint","IMPRINT",EDGE,{"derivedFrom":sQuery(id+"F43.wireOp",EDGE,"E72")}),1.0]])]});
            var Q5;
            Q5=makeQuery(id+"F43.imprint","IMPRINT",FACE,{"disambiguationData":[TD([[makeQuery(id+"F43.imprint","IMPRINT",EDGE,{"derivedFrom":sQuery(id+"F43.wireOp",EDGE,"E73")}),1.0]])]});
            var Q6;
            Q6=makeQuery(id+"F43.imprint","IMPRINT",FACE,{"disambiguationData":[TD([[makeQuery(id+"F43.imprint","IMPRINT",EDGE,{"derivedFrom":sQuery(id+"F43.wireOp",EDGE,"E74")}),1.0]])]});
            var Q7;
            Q7=makeQuery(id+"F43.imprint","IMPRINT",FACE,{"disambiguationData":[TD([[makeQuery(id+"F43.imprint","IMPRINT",EDGE,{"derivedFrom":sQuery(id+"F43.wireOp",EDGE,"E70")}),1.0]])]});
            var Q8;
            Q8=makeQuery(id+"F43.imprint","IMPRINT",FACE,{"disambiguationData":[TD([[makeQuery(id+"F43.imprint","IMPRINT",EDGE,{"derivedFrom":sQuery(id+"F43.wireOp",EDGE,"E69")}),1.0]])]});
            extrude(context, id + "F44", {"entities" : qUnion([Q0, Q1, Q2, Q3, Q4, Q5, Q6, Q7, Q8]), "operationType" : NewBodyOperationType.REMOVE, "endBound" : BoundingType.THROUGH_ALL, "oppositeDirection" : true, "depth" : 25 * mm, "offsetDistance" : 25 * mm});
        }
        {
            var Q0;
            Q0=makeQuery(id+"F40.opExtrude","CAP_EDGE",EDGE,{"disambiguationData":[OSD([sQuery(id+"F39.wireOp",EDGE,"E62")])],"isStart":true});
            var Q1;
            Q1=makeQuery(id+"F40.opExtrude","CAP_EDGE",EDGE,{"disambiguationData":[OSD([sQuery(id+"F39.wireOp",EDGE,"E61")])],"isStart":true});
            var Q2;
            Q2=makeQuery(id+"F40.opExtrude","CAP_EDGE",EDGE,{"disambiguationData":[OSD([sQuery(id+"F39.wireOp",EDGE,"E63")])],"isStart":true});
            var Q3;
            Q3=makeQuery(id+"F40.boolean.opBoolean","COPY",EDGE,{"derivedFrom":makeQuery(id+"F40.opExtrude","CAP_EDGE",EDGE,{"disambiguationData":[OSD([sQuery(id+"F39.wireOp",EDGE,"E64")])],"isStart":true})});
            var Q4;
            Q4=makeQuery(id+"F42.opExtrude","CAP_EDGE",EDGE,{"disambiguationData":[OSD([sQuery(id+"F41.wireOp",EDGE,"E66")])],"isStart":true});
            var Q5;
            Q5=makeQuery(id+"F42.boolean.opBoolean","COPY",EDGE,{"derivedFrom":makeQuery(id+"F42.opExtrude","CAP_EDGE",EDGE,{"disambiguationData":[OSD([sQuery(id+"F41.wireOp",EDGE,"E65")])],"isStart":true})});
            var Q6;
            Q6=makeQuery(id+"F44.boolean.opBoolean","COPY",EDGE,{"derivedFrom":makeQuery(id+"F44.opExtrude","CAP_EDGE",EDGE,{"disambiguationData":[OSD([sQuery(id+"F43.wireOp",EDGE,"E67")])],"isStart":true})});
            var Q7;
            Q7=makeQuery(id+"F44.boolean.opBoolean","COPY",EDGE,{"derivedFrom":makeQuery(id+"F44.opExtrude","CAP_EDGE",EDGE,{"disambiguationData":[OSD([sQuery(id+"F43.wireOp",EDGE,"E71")])],"isStart":true})});
            var Q8;
            Q8=makeQuery(id+"F44.boolean.opBoolean","COPY",EDGE,{"derivedFrom":makeQuery(id+"F44.opExtrude","CAP_EDGE",EDGE,{"disambiguationData":[OSD([sQuery(id+"F43.wireOp",EDGE,"E68")])],"isStart":true})});
            var Q9;
            Q9=makeQuery(id+"F44.boolean.opBoolean","COPY",EDGE,{"derivedFrom":makeQuery(id+"F44.opExtrude","CAP_EDGE",EDGE,{"disambiguationData":[OSD([sQuery(id+"F43.wireOp",EDGE,"E72")])],"isStart":true})});
            var Q10;
            Q10=makeQuery(id+"F44.boolean.opBoolean","COPY",EDGE,{"derivedFrom":makeQuery(id+"F44.opExtrude","CAP_EDGE",EDGE,{"disambiguationData":[OSD([sQuery(id+"F43.wireOp",EDGE,"E69")])],"isStart":true})});
            var Q11;
            Q11=makeQuery(id+"F44.boolean.opBoolean","COPY",EDGE,{"derivedFrom":makeQuery(id+"F44.opExtrude","CAP_EDGE",EDGE,{"disambiguationData":[OSD([sQuery(id+"F43.wireOp",EDGE,"E73")])],"isStart":true})});
            var Q12;
            Q12=makeQuery(id+"F44.boolean.opBoolean","COPY",EDGE,{"derivedFrom":makeQuery(id+"F44.opExtrude","CAP_EDGE",EDGE,{"disambiguationData":[OSD([sQuery(id+"F43.wireOp",EDGE,"E70")])],"isStart":true})});
            var Q13;
            Q13=makeQuery(id+"F44.boolean.opBoolean","COPY",EDGE,{"derivedFrom":makeQuery(id+"F44.opExtrude","CAP_EDGE",EDGE,{"disambiguationData":[OSD([sQuery(id+"F43.wireOp",EDGE,"E74")])],"isStart":true})});
            var Q14;
            Q14=makeQuery(id+"F42.boolean.opBoolean","INTERSECT",EDGE,{"derivedFrom":[makeQuery(id+"F38.opPattern","COPY",FACE,{"derivedFrom":makeQuery(id+"F6.opExtrude","SWEPT_FACE",FACE,{"disambiguationData":[OSD([sQuery(id+"F5.wireOp",EDGE,"E0.right")])]}),"instanceName":"1"}),makeQuery(id+"F42.opExtrude","SWEPT_FACE",FACE,{"disambiguationData":[OSD([sQuery(id+"F41.wireOp",EDGE,"E66")])]})]});
            var Q15;
            Q15=makeQuery(id+"F42.boolean.opBoolean","INTERSECT",EDGE,{"derivedFrom":[makeQuery(id+"F38.opPattern","COPY",FACE,{"derivedFrom":makeQuery(id+"F37.opPattern","COPY",FACE,{"derivedFrom":makeQuery(id+"F6.opExtrude","SWEPT_FACE",FACE,{"disambiguationData":[OSD([sQuery(id+"F5.wireOp",EDGE,"E0.right")])]}),"instanceName":"1"}),"instanceName":"1"}),makeQuery(id+"F42.opExtrude","SWEPT_FACE",FACE,{"disambiguationData":[OSD([sQuery(id+"F41.wireOp",EDGE,"E65")])]})]});
            var Q16;
            Q16=makeQuery(id+"F40.boolean.opBoolean","INTERSECT",EDGE,{"derivedFrom":[makeQuery(id+"F38.opPattern","COPY",FACE,{"derivedFrom":makeQuery(id+"F37.opPattern","COPY",FACE,{"derivedFrom":makeQuery(id+"F6.opExtrude","SWEPT_FACE",FACE,{"disambiguationData":[OSD([sQuery(id+"F5.wireOp",EDGE,"E0.bottom")])]}),"instanceName":"1"}),"instanceName":"1"}),makeQuery(id+"F40.opExtrude","SWEPT_FACE",FACE,{"disambiguationData":[OSD([sQuery(id+"F39.wireOp",EDGE,"E64")])]})]});
            var Q17;
            Q17=makeQuery(id+"F40.boolean.opBoolean","INTERSECT",EDGE,{"derivedFrom":[makeQuery(id+"F38.opPattern","COPY",FACE,{"derivedFrom":makeQuery(id+"F37.opPattern","COPY",FACE,{"derivedFrom":makeQuery(id+"F30.opPattern","COPY",FACE,{"derivedFrom":makeQuery(id+"F29.opPattern","COPY",FACE,{"derivedFrom":makeQuery(id+"F6.opExtrude","SWEPT_FACE",FACE,{"disambiguationData":[OSD([sQuery(id+"F5.wireOp",EDGE,"E0.top")])]}),"instanceName":"1"}),"instanceName":"1"}),"instanceName":"1"}),"instanceName":"1"}),makeQuery(id+"F40.opExtrude","SWEPT_FACE",FACE,{"disambiguationData":[OSD([sQuery(id+"F39.wireOp",EDGE,"E63")])]})]});
            var Q18;
            Q18=makeQuery(id+"F40.boolean.opBoolean","INTERSECT",EDGE,{"derivedFrom":[makeQuery(id+"F37.opPattern","COPY",FACE,{"derivedFrom":makeQuery(id+"F30.opPattern","COPY",FACE,{"derivedFrom":makeQuery(id+"F29.opPattern","COPY",FACE,{"derivedFrom":makeQuery(id+"F6.opExtrude","SWEPT_FACE",FACE,{"disambiguationData":[OSD([sQuery(id+"F5.wireOp",EDGE,"E0.top")])]}),"instanceName":"1"}),"instanceName":"1"}),"instanceName":"1"}),makeQuery(id+"F40.opExtrude","SWEPT_FACE",FACE,{"disambiguationData":[OSD([sQuery(id+"F39.wireOp",EDGE,"E61")])]})]});
            var Q19;
            Q19=makeQuery(id+"F40.boolean.opBoolean","INTERSECT",EDGE,{"derivedFrom":[makeQuery(id+"F37.opPattern","COPY",FACE,{"derivedFrom":makeQuery(id+"F6.opExtrude","SWEPT_FACE",FACE,{"disambiguationData":[OSD([sQuery(id+"F5.wireOp",EDGE,"E0.bottom")])]}),"instanceName":"1"}),makeQuery(id+"F40.opExtrude","SWEPT_FACE",FACE,{"disambiguationData":[OSD([sQuery(id+"F39.wireOp",EDGE,"E62")])]})]});
            var Q20;
            Q20=makeQuery(id+"F44.boolean.opBoolean","INTERSECT",EDGE,{"derivedFrom":[makeQuery(id+"F38.opPattern","COPY",FACE,{"derivedFrom":makeQuery(id+"F37.opPattern","COPY",FACE,{"derivedFrom":makeQuery(id+"F6.opExtrude","CAP_FACE",FACE,{"disambiguationData":[OSD([sQuery(id+"F5.wireOp",EDGE,"E0.bottom"),sQuery(id+"F5.wireOp",EDGE,"E0.top"),sQuery(id+"F5.wireOp",EDGE,"E0.left"),sQuery(id+"F5.wireOp",EDGE,"E0.right")])],"isStart":true}),"instanceName":"1"}),"instanceName":"1"}),makeQuery(id+"F44.opExtrude","SWEPT_FACE",FACE,{"disambiguationData":[OSD([sQuery(id+"F43.wireOp",EDGE,"E70")])]})]});
            var Q21;
            Q21=makeQuery(id+"F44.boolean.opBoolean","INTERSECT",EDGE,{"derivedFrom":[makeQuery(id+"F38.opPattern","COPY",FACE,{"derivedFrom":makeQuery(id+"F37.opPattern","COPY",FACE,{"derivedFrom":makeQuery(id+"F30.opPattern","COPY",FACE,{"derivedFrom":makeQuery(id+"F29.opPattern","COPY",FACE,{"derivedFrom":makeQuery(id+"F6.opExtrude","SWEPT_FACE",FACE,{"disambiguationData":[OSD([sQuery(id+"F5.wireOp",EDGE,"E0.left")])]}),"instanceName":"1"}),"instanceName":"1"}),"instanceName":"1"}),"instanceName":"1"}),makeQuery(id+"F44.opExtrude","SWEPT_FACE",FACE,{"disambiguationData":[OSD([sQuery(id+"F43.wireOp",EDGE,"E69")])]})]});
            var Q22;
            Q22=makeQuery(id+"F44.boolean.opBoolean","INTERSECT",EDGE,{"derivedFrom":[makeQuery(id+"F37.opPattern","COPY",FACE,{"derivedFrom":makeQuery(id+"F30.opPattern","COPY",FACE,{"derivedFrom":makeQuery(id+"F29.opPattern","COPY",FACE,{"derivedFrom":makeQuery(id+"F6.opExtrude","SWEPT_FACE",FACE,{"disambiguationData":[OSD([sQuery(id+"F5.wireOp",EDGE,"E0.left")])]}),"instanceName":"1"}),"instanceName":"1"}),"instanceName":"1"}),makeQuery(id+"F44.opExtrude","SWEPT_FACE",FACE,{"disambiguationData":[OSD([sQuery(id+"F43.wireOp",EDGE,"E68")])]})]});
            var Q23;
            Q23=makeQuery(id+"F44.boolean.opBoolean","INTERSECT",EDGE,{"derivedFrom":[makeQuery(id+"F37.opPattern","COPY",FACE,{"derivedFrom":makeQuery(id+"F6.opExtrude","CAP_FACE",FACE,{"disambiguationData":[OSD([sQuery(id+"F5.wireOp",EDGE,"E0.bottom"),sQuery(id+"F5.wireOp",EDGE,"E0.top"),sQuery(id+"F5.wireOp",EDGE,"E0.left"),sQuery(id+"F5.wireOp",EDGE,"E0.right")])],"isStart":true}),"instanceName":"1"}),makeQuery(id+"F44.opExtrude","SWEPT_FACE",FACE,{"disambiguationData":[OSD([sQuery(id+"F43.wireOp",EDGE,"E67")])]})]});
            var Q24;
            Q24=makeQuery(id+"F44.boolean.opBoolean","INTERSECT",EDGE,{"derivedFrom":[makeQuery(id+"F38.opPattern","COPY",FACE,{"derivedFrom":makeQuery(id+"F6.opExtrude","CAP_FACE",FACE,{"disambiguationData":[OSD([sQuery(id+"F5.wireOp",EDGE,"E0.bottom"),sQuery(id+"F5.wireOp",EDGE,"E0.top"),sQuery(id+"F5.wireOp",EDGE,"E0.left"),sQuery(id+"F5.wireOp",EDGE,"E0.right")])],"isStart":true}),"instanceName":"1"}),makeQuery(id+"F44.opExtrude","SWEPT_FACE",FACE,{"disambiguationData":[OSD([sQuery(id+"F43.wireOp",EDGE,"E74")])]})]});
            var Q25;
            Q25=makeQuery(id+"F44.boolean.opBoolean","INTERSECT",EDGE,{"derivedFrom":[makeQuery(id+"F38.opPattern","COPY",FACE,{"derivedFrom":makeQuery(id+"F30.opPattern","COPY",FACE,{"derivedFrom":makeQuery(id+"F29.opPattern","COPY",FACE,{"derivedFrom":makeQuery(id+"F6.opExtrude","SWEPT_FACE",FACE,{"disambiguationData":[OSD([sQuery(id+"F5.wireOp",EDGE,"E0.left")])]}),"instanceName":"1"}),"instanceName":"1"}),"instanceName":"1"}),makeQuery(id+"F44.opExtrude","SWEPT_FACE",FACE,{"disambiguationData":[OSD([sQuery(id+"F43.wireOp",EDGE,"E73")])]})]});
            var Q26;
            Q26=makeQuery(id+"F44.boolean.opBoolean","INTERSECT",EDGE,{"derivedFrom":[makeQuery(id+"F30.opPattern","COPY",FACE,{"derivedFrom":makeQuery(id+"F29.opPattern","COPY",FACE,{"derivedFrom":makeQuery(id+"F6.opExtrude","SWEPT_FACE",FACE,{"disambiguationData":[OSD([sQuery(id+"F5.wireOp",EDGE,"E0.left")])]}),"instanceName":"1"}),"instanceName":"1"}),makeQuery(id+"F44.opExtrude","SWEPT_FACE",FACE,{"disambiguationData":[OSD([sQuery(id+"F43.wireOp",EDGE,"E72")])]})]});
            var Q27;
            Q27=makeQuery(id+"F44.boolean.opBoolean","INTERSECT",EDGE,{"derivedFrom":[makeQuery(id+"F6.opExtrude","CAP_FACE",FACE,{"disambiguationData":[OSD([sQuery(id+"F5.wireOp",EDGE,"E0.bottom"),sQuery(id+"F5.wireOp",EDGE,"E0.top"),sQuery(id+"F5.wireOp",EDGE,"E0.left"),sQuery(id+"F5.wireOp",EDGE,"E0.right")])],"isStart":true}),makeQuery(id+"F44.opExtrude","SWEPT_FACE",FACE,{"disambiguationData":[OSD([sQuery(id+"F43.wireOp",EDGE,"E71")])]})]});
            var Q28;
            Q28=makeQuery(id+"F40.boolean.opBoolean","INTERSECT",EDGE,{"derivedFrom":[makeQuery(id+"F38.opPattern","COPY",FACE,{"derivedFrom":makeQuery(id+"F6.opExtrude","SWEPT_FACE",FACE,{"disambiguationData":[OSD([sQuery(id+"F5.wireOp",EDGE,"E0.top")])]}),"instanceName":"1"}),makeQuery(id+"F40.opExtrude","SWEPT_FACE",FACE,{"disambiguationData":[OSD([sQuery(id+"F39.wireOp",EDGE,"E64")])]})]});
            var Q29;
            Q29=makeQuery(id+"F40.boolean.opBoolean","INTERSECT",EDGE,{"derivedFrom":[makeQuery(id+"F38.opPattern","COPY",FACE,{"derivedFrom":makeQuery(id+"F30.opPattern","COPY",FACE,{"derivedFrom":makeQuery(id+"F29.opPattern","COPY",FACE,{"derivedFrom":makeQuery(id+"F6.opExtrude","SWEPT_FACE",FACE,{"disambiguationData":[OSD([sQuery(id+"F5.wireOp",EDGE,"E0.bottom")])]}),"instanceName":"1"}),"instanceName":"1"}),"instanceName":"1"}),makeQuery(id+"F40.opExtrude","SWEPT_FACE",FACE,{"disambiguationData":[OSD([sQuery(id+"F39.wireOp",EDGE,"E63")])]})]});
            var Q30;
            Q30=makeQuery(id+"F40.boolean.opBoolean","INTERSECT",EDGE,{"derivedFrom":[makeQuery(id+"F30.opPattern","COPY",FACE,{"derivedFrom":makeQuery(id+"F29.opPattern","COPY",FACE,{"derivedFrom":makeQuery(id+"F6.opExtrude","SWEPT_FACE",FACE,{"disambiguationData":[OSD([sQuery(id+"F5.wireOp",EDGE,"E0.bottom")])]}),"instanceName":"1"}),"instanceName":"1"}),makeQuery(id+"F40.opExtrude","SWEPT_FACE",FACE,{"disambiguationData":[OSD([sQuery(id+"F39.wireOp",EDGE,"E61")])]})]});
            var Q31;
            Q31=makeQuery(id+"F40.boolean.opBoolean","INTERSECT",EDGE,{"derivedFrom":[makeQuery(id+"F6.opExtrude","SWEPT_FACE",FACE,{"disambiguationData":[OSD([sQuery(id+"F5.wireOp",EDGE,"E0.top")])]}),makeQuery(id+"F40.opExtrude","SWEPT_FACE",FACE,{"disambiguationData":[OSD([sQuery(id+"F39.wireOp",EDGE,"E62")])]})]});
            var Q32;
            Q32=makeQuery(id+"F40.boolean.opBoolean","INTERSECT",EDGE,{"derivedFrom":[makeQuery(id+"F38.opPattern","COPY",FACE,{"derivedFrom":makeQuery(id+"F37.opPattern","COPY",FACE,{"derivedFrom":makeQuery(id+"F30.opPattern","COPY",FACE,{"derivedFrom":makeQuery(id+"F29.opPattern","COPY",FACE,{"derivedFrom":makeQuery(id+"F6.opExtrude","SWEPT_FACE",FACE,{"disambiguationData":[OSD([sQuery(id+"F5.wireOp",EDGE,"E0.bottom")])]}),"instanceName":"1"}),"instanceName":"1"}),"instanceName":"1"}),"instanceName":"1"}),makeQuery(id+"F40.opExtrude","SWEPT_FACE",FACE,{"disambiguationData":[OSD([sQuery(id+"F39.wireOp",EDGE,"E63")])]})]});
            var Q33;
            Q33=makeQuery(id+"F40.boolean.opBoolean","INTERSECT",EDGE,{"derivedFrom":[makeQuery(id+"F38.opPattern","COPY",FACE,{"derivedFrom":makeQuery(id+"F37.opPattern","COPY",FACE,{"derivedFrom":makeQuery(id+"F6.opExtrude","SWEPT_FACE",FACE,{"disambiguationData":[OSD([sQuery(id+"F5.wireOp",EDGE,"E0.top")])]}),"instanceName":"1"}),"instanceName":"1"}),makeQuery(id+"F40.opExtrude","SWEPT_FACE",FACE,{"disambiguationData":[OSD([sQuery(id+"F39.wireOp",EDGE,"E64")])]})]});
            var Q34;
            Q34=makeQuery(id+"F40.boolean.opBoolean","INTERSECT",EDGE,{"derivedFrom":[makeQuery(id+"F37.opPattern","COPY",FACE,{"derivedFrom":makeQuery(id+"F6.opExtrude","SWEPT_FACE",FACE,{"disambiguationData":[OSD([sQuery(id+"F5.wireOp",EDGE,"E0.top")])]}),"instanceName":"1"}),makeQuery(id+"F40.opExtrude","SWEPT_FACE",FACE,{"disambiguationData":[OSD([sQuery(id+"F39.wireOp",EDGE,"E62")])]})]});
            var Q35;
            Q35=makeQuery(id+"F40.boolean.opBoolean","INTERSECT",EDGE,{"derivedFrom":[makeQuery(id+"F37.opPattern","COPY",FACE,{"derivedFrom":makeQuery(id+"F30.opPattern","COPY",FACE,{"derivedFrom":makeQuery(id+"F29.opPattern","COPY",FACE,{"derivedFrom":makeQuery(id+"F6.opExtrude","SWEPT_FACE",FACE,{"disambiguationData":[OSD([sQuery(id+"F5.wireOp",EDGE,"E0.bottom")])]}),"instanceName":"1"}),"instanceName":"1"}),"instanceName":"1"}),makeQuery(id+"F40.opExtrude","SWEPT_FACE",FACE,{"disambiguationData":[OSD([sQuery(id+"F39.wireOp",EDGE,"E61")])]})]});
            var Q36;
            Q36=makeQuery(id+"F42.boolean.opBoolean","INTERSECT",EDGE,{"derivedFrom":[makeQuery(id+"F37.opPattern","COPY",FACE,{"derivedFrom":makeQuery(id+"F6.opExtrude","SWEPT_FACE",FACE,{"disambiguationData":[OSD([sQuery(id+"F5.wireOp",EDGE,"E0.left")])]}),"instanceName":"1"}),makeQuery(id+"F42.opExtrude","SWEPT_FACE",FACE,{"disambiguationData":[OSD([sQuery(id+"F41.wireOp",EDGE,"E65")])]})]});
            var Q37;
            Q37=makeQuery(id+"F42.boolean.opBoolean","INTERSECT",EDGE,{"derivedFrom":[makeQuery(id+"F37.opPattern","COPY",FACE,{"derivedFrom":makeQuery(id+"F30.opPattern","COPY",FACE,{"derivedFrom":makeQuery(id+"F29.opPattern","COPY",FACE,{"derivedFrom":makeQuery(id+"F6.opExtrude","CAP_FACE",FACE,{"disambiguationData":[OSD([sQuery(id+"F5.wireOp",EDGE,"E0.bottom"),sQuery(id+"F5.wireOp",EDGE,"E0.top"),sQuery(id+"F5.wireOp",EDGE,"E0.left"),sQuery(id+"F5.wireOp",EDGE,"E0.right")])],"isStart":true}),"instanceName":"1"}),"instanceName":"1"}),"instanceName":"1"}),makeQuery(id+"F42.opExtrude","SWEPT_FACE",FACE,{"disambiguationData":[OSD([sQuery(id+"F41.wireOp",EDGE,"E65")])]})]});
            var Q38;
            Q38=makeQuery(id+"F42.boolean.opBoolean","INTERSECT",EDGE,{"derivedFrom":[makeQuery(id+"F6.opExtrude","SWEPT_FACE",FACE,{"disambiguationData":[OSD([sQuery(id+"F5.wireOp",EDGE,"E0.left")])]}),makeQuery(id+"F42.opExtrude","SWEPT_FACE",FACE,{"disambiguationData":[OSD([sQuery(id+"F41.wireOp",EDGE,"E66")])]})]});
            var Q39;
            Q39=makeQuery(id+"F42.boolean.opBoolean","INTERSECT",EDGE,{"derivedFrom":[makeQuery(id+"F30.opPattern","COPY",FACE,{"derivedFrom":makeQuery(id+"F29.opPattern","COPY",FACE,{"derivedFrom":makeQuery(id+"F6.opExtrude","CAP_FACE",FACE,{"disambiguationData":[OSD([sQuery(id+"F5.wireOp",EDGE,"E0.bottom"),sQuery(id+"F5.wireOp",EDGE,"E0.top"),sQuery(id+"F5.wireOp",EDGE,"E0.left"),sQuery(id+"F5.wireOp",EDGE,"E0.right")])],"isStart":true}),"instanceName":"1"}),"instanceName":"1"}),makeQuery(id+"F42.opExtrude","SWEPT_FACE",FACE,{"disambiguationData":[OSD([sQuery(id+"F41.wireOp",EDGE,"E66")])]})]});
            var Q40;
            Q40=makeQuery(id+"F42.boolean.opBoolean","INTERSECT",EDGE,{"derivedFrom":[makeQuery(id+"F38.opPattern","COPY",FACE,{"derivedFrom":makeQuery(id+"F37.opPattern","COPY",FACE,{"derivedFrom":makeQuery(id+"F30.opPattern","COPY",FACE,{"derivedFrom":makeQuery(id+"F29.opPattern","COPY",FACE,{"derivedFrom":makeQuery(id+"F6.opExtrude","CAP_FACE",FACE,{"disambiguationData":[OSD([sQuery(id+"F5.wireOp",EDGE,"E0.bottom"),sQuery(id+"F5.wireOp",EDGE,"E0.top"),sQuery(id+"F5.wireOp",EDGE,"E0.left"),sQuery(id+"F5.wireOp",EDGE,"E0.right")])],"isStart":false}),"instanceName":"1"}),"instanceName":"1"}),"instanceName":"1"}),"instanceName":"1"}),makeQuery(id+"F42.opExtrude","SWEPT_FACE",FACE,{"disambiguationData":[OSD([sQuery(id+"F41.wireOp",EDGE,"E65")])]})]});
            var Q41;
            Q41=makeQuery(id+"F42.boolean.opBoolean","INTERSECT",EDGE,{"derivedFrom":[makeQuery(id+"F37.opPattern","COPY",FACE,{"derivedFrom":makeQuery(id+"F30.opPattern","COPY",FACE,{"derivedFrom":makeQuery(id+"F29.opPattern","COPY",FACE,{"derivedFrom":makeQuery(id+"F6.opExtrude","CAP_FACE",FACE,{"disambiguationData":[OSD([sQuery(id+"F5.wireOp",EDGE,"E0.bottom"),sQuery(id+"F5.wireOp",EDGE,"E0.top"),sQuery(id+"F5.wireOp",EDGE,"E0.left"),sQuery(id+"F5.wireOp",EDGE,"E0.right")])],"isStart":false}),"instanceName":"1"}),"instanceName":"1"}),"instanceName":"1"}),makeQuery(id+"F42.opExtrude","SWEPT_FACE",FACE,{"disambiguationData":[OSD([sQuery(id+"F41.wireOp",EDGE,"E65")])]})]});
            var Q42;
            Q42=makeQuery(id+"F42.boolean.opBoolean","INTERSECT",EDGE,{"derivedFrom":[makeQuery(id+"F30.opPattern","COPY",FACE,{"derivedFrom":makeQuery(id+"F29.opPattern","COPY",FACE,{"derivedFrom":makeQuery(id+"F6.opExtrude","CAP_FACE",FACE,{"disambiguationData":[OSD([sQuery(id+"F5.wireOp",EDGE,"E0.bottom"),sQuery(id+"F5.wireOp",EDGE,"E0.top"),sQuery(id+"F5.wireOp",EDGE,"E0.left"),sQuery(id+"F5.wireOp",EDGE,"E0.right")])],"isStart":false}),"instanceName":"1"}),"instanceName":"1"}),makeQuery(id+"F42.opExtrude","SWEPT_FACE",FACE,{"disambiguationData":[OSD([sQuery(id+"F41.wireOp",EDGE,"E66")])]})]});
            var Q43;
            Q43=makeQuery(id+"F42.boolean.opBoolean","INTERSECT",EDGE,{"derivedFrom":[makeQuery(id+"F38.opPattern","COPY",FACE,{"derivedFrom":makeQuery(id+"F6.opExtrude","SWEPT_FACE",FACE,{"disambiguationData":[OSD([sQuery(id+"F5.wireOp",EDGE,"E0.left")])]}),"instanceName":"1"}),makeQuery(id+"F42.opExtrude","SWEPT_FACE",FACE,{"disambiguationData":[OSD([sQuery(id+"F41.wireOp",EDGE,"E66")])]})]});
            var Q44;
            Q44=makeQuery(id+"F42.boolean.opBoolean","INTERSECT",EDGE,{"derivedFrom":[makeQuery(id+"F38.opPattern","COPY",FACE,{"derivedFrom":makeQuery(id+"F30.opPattern","COPY",FACE,{"derivedFrom":makeQuery(id+"F29.opPattern","COPY",FACE,{"derivedFrom":makeQuery(id+"F6.opExtrude","CAP_FACE",FACE,{"disambiguationData":[OSD([sQuery(id+"F5.wireOp",EDGE,"E0.bottom"),sQuery(id+"F5.wireOp",EDGE,"E0.top"),sQuery(id+"F5.wireOp",EDGE,"E0.left"),sQuery(id+"F5.wireOp",EDGE,"E0.right")])],"isStart":false}),"instanceName":"1"}),"instanceName":"1"}),"instanceName":"1"}),makeQuery(id+"F42.opExtrude","SWEPT_FACE",FACE,{"disambiguationData":[OSD([sQuery(id+"F41.wireOp",EDGE,"E66")])]})]});
            var Q45;
            Q45=makeQuery(id+"F42.boolean.opBoolean","INTERSECT",EDGE,{"derivedFrom":[makeQuery(id+"F38.opPattern","COPY",FACE,{"derivedFrom":makeQuery(id+"F30.opPattern","COPY",FACE,{"derivedFrom":makeQuery(id+"F29.opPattern","COPY",FACE,{"derivedFrom":makeQuery(id+"F6.opExtrude","CAP_FACE",FACE,{"disambiguationData":[OSD([sQuery(id+"F5.wireOp",EDGE,"E0.bottom"),sQuery(id+"F5.wireOp",EDGE,"E0.top"),sQuery(id+"F5.wireOp",EDGE,"E0.left"),sQuery(id+"F5.wireOp",EDGE,"E0.right")])],"isStart":true}),"instanceName":"1"}),"instanceName":"1"}),"instanceName":"1"}),makeQuery(id+"F42.opExtrude","SWEPT_FACE",FACE,{"disambiguationData":[OSD([sQuery(id+"F41.wireOp",EDGE,"E66")])]})]});
            var Q46;
            Q46=makeQuery(id+"F42.boolean.opBoolean","INTERSECT",EDGE,{"derivedFrom":[makeQuery(id+"F38.opPattern","COPY",FACE,{"derivedFrom":makeQuery(id+"F37.opPattern","COPY",FACE,{"derivedFrom":makeQuery(id+"F6.opExtrude","SWEPT_FACE",FACE,{"disambiguationData":[OSD([sQuery(id+"F5.wireOp",EDGE,"E0.left")])]}),"instanceName":"1"}),"instanceName":"1"}),makeQuery(id+"F42.opExtrude","SWEPT_FACE",FACE,{"disambiguationData":[OSD([sQuery(id+"F41.wireOp",EDGE,"E65")])]})]});
            var Q47;
            Q47=makeQuery(id+"F42.boolean.opBoolean","INTERSECT",EDGE,{"derivedFrom":[makeQuery(id+"F38.opPattern","COPY",FACE,{"derivedFrom":makeQuery(id+"F37.opPattern","COPY",FACE,{"derivedFrom":makeQuery(id+"F30.opPattern","COPY",FACE,{"derivedFrom":makeQuery(id+"F29.opPattern","COPY",FACE,{"derivedFrom":makeQuery(id+"F6.opExtrude","CAP_FACE",FACE,{"disambiguationData":[OSD([sQuery(id+"F5.wireOp",EDGE,"E0.bottom"),sQuery(id+"F5.wireOp",EDGE,"E0.top"),sQuery(id+"F5.wireOp",EDGE,"E0.left"),sQuery(id+"F5.wireOp",EDGE,"E0.right")])],"isStart":true}),"instanceName":"1"}),"instanceName":"1"}),"instanceName":"1"}),"instanceName":"1"}),makeQuery(id+"F42.opExtrude","SWEPT_FACE",FACE,{"disambiguationData":[OSD([sQuery(id+"F41.wireOp",EDGE,"E65")])]})]});
            var Q48;
            Q48=makeQuery(id+"F40.boolean.opBoolean","COPY",EDGE,{"derivedFrom":makeQuery(id+"F40.opExtrude","CAP_EDGE",EDGE,{"disambiguationData":[OSD([sQuery(id+"F39.wireOp",EDGE,"E62")])],"isStart":true})});
            var Q49;
            Q49=makeQuery(id+"F40.opExtrude","CAP_EDGE",EDGE,{"disambiguationData":[OSD([sQuery(id+"F39.wireOp",EDGE,"E64")])],"isStart":true});
            chamfer(context, id + "F45", {"entities" : qUnion([Q0, Q1, Q2, Q3, Q4, Q5, Q6, Q7, Q8, Q9, Q10, Q11, Q12, Q13, Q14, Q15, Q16, Q17, Q18, Q19, Q20, Q21, Q22, Q23, Q24, Q25, Q26, Q27, Q28, Q29, Q30, Q31, Q32, Q33, Q34, Q35, Q36, Q37, Q38, Q39, Q40, Q41, Q42, Q43, Q44, Q45, Q46, Q47, Q48, Q49]), "width" : 1.8 * mm, "tangentPropagation" : true});
        }
    });
